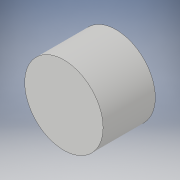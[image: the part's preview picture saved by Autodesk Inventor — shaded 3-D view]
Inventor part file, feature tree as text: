
AUTODESK INVENTOR PART (.ipt)
format: ipt  version: 2017 (Build 210142000, 142)  size: 89,600 bytes
history: native  units: in
note: dims shown in document units (in); Inventor stores cm internally (conversion verified against a paired STEP export)
features: extrude x1, sketch x1
ambient origin geometry x8: Origin, YZ Plane, XZ Plane, XY Plane, X Axis, Y Axis, Z Axis, Center Point
bodies: Solid1 (feature_tree)
feature tree (2):
  extrude  "Extrusion1"  Depth=1.0in TaperAngle=0.0deg
  sketch  "Sketch1"  dims[d0=1.5in d1=1.0in d2=0.0in]
